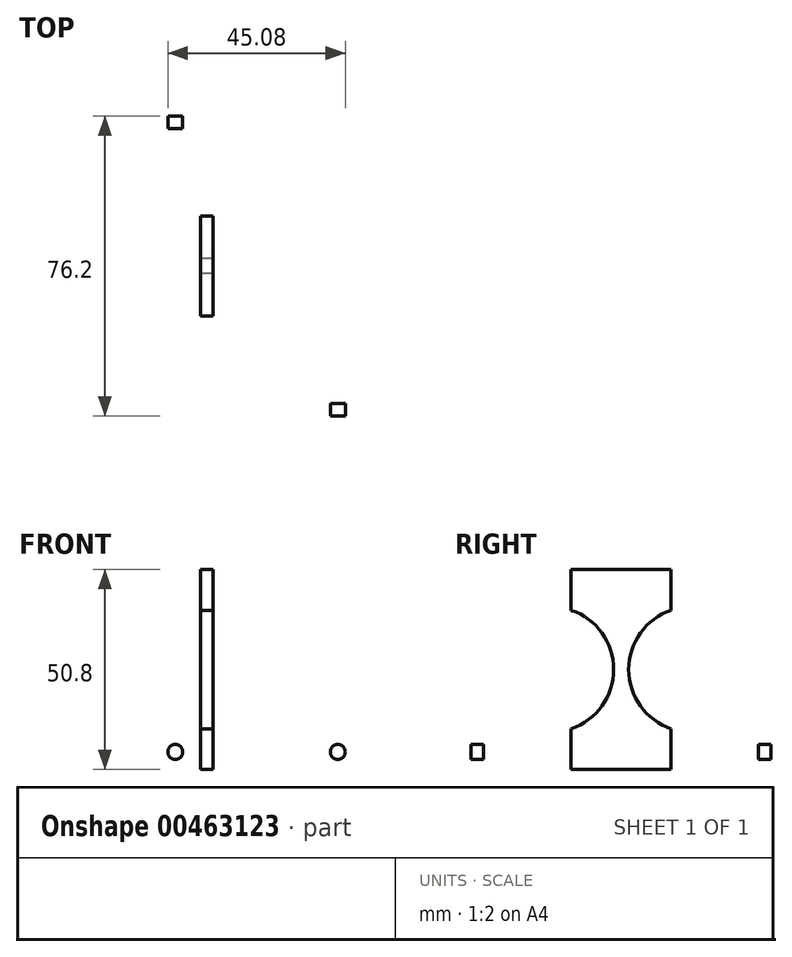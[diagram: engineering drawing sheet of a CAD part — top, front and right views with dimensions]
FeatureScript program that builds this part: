
annotation { "Feature Type Name" : "Feature", "Feature Type Description" : "" }
export const myFeature = defineFeature(function(context is Context, id is Id, definition is map)
    precondition{}
    {
        {
            var Q0;
            Q0=qCreatedBy(makeId("Top.planeOp"),FACE);
            var sketch = newSketch(context, id + "F0", { "sketchPlane" : qUnion([Q0])});
            skLineSegment(sketch, "E0.bottom", {"start": v(1.59, -38.1) * mm, "end": v(-1.59, -38.1) * mm});
            skLineSegment(sketch, "E0.top", {"start": v(1.59, 38.1) * mm, "end": v(-1.59, 38.1) * mm});
            skLineSegment(sketch, "E0.left", {"start": v(1.59, -38.1) * mm, "end": v(1.59, 38.1) * mm});
            skLineSegment(sketch, "E0.right", {"start": v(-1.59, -38.1) * mm, "end": v(-1.59, 38.1) * mm});
            skPoint(sketch, "E0.middle", {"position": v(0, 0) * mm});
            skLineSegment(sketch, "E1.bottom", {"start": v(1.59, -38.1) * mm, "end": v(39.69, -38.1) * mm});
            skLineSegment(sketch, "E1.top", {"start": v(1.59, -34.93) * mm, "end": v(39.69, -34.92) * mm});
            skLineSegment(sketch, "E1.left", {"start": v(1.59, -38.1) * mm, "end": v(1.59, -34.93) * mm});
            skLineSegment(sketch, "E1.right", {"start": v(39.69, -38.1) * mm, "end": v(39.69, -34.93) * mm});
            skLineSegment(sketch, "E2.bottom", {"start": v(-1.59, 38.1) * mm, "end": v(-14.29, 38.1) * mm});
            skLineSegment(sketch, "E2.top", {"start": v(-1.59, 34.93) * mm, "end": v(-14.29, 34.93) * mm});
            skLineSegment(sketch, "E2.left", {"start": v(-1.59, 38.1) * mm, "end": v(-1.59, 34.93) * mm});
            skLineSegment(sketch, "E2.right", {"start": v(-14.29, 38.1) * mm, "end": v(-14.29, 34.93) * mm});
            skSolve(sketch);
        }
        {
            var Q0;
            Q0=makeQuery(id+"F0.imprint","IMPRINT",FACE,{"disambiguationData":[TD([[makeQuery(id+"F0.imprint","IMPRINT",EDGE,{"derivedFrom":sQuery(id+"F0.wireOp",EDGE,"E1.bottom")}),1.0]])]});
            var Q1;
            Q1=makeQuery(id+"F0.imprint","IMPRINT",FACE,{"disambiguationData":[TD([[makeQuery(id+"F0.imprint","IMPRINT",EDGE,{"derivedFrom":sQuery(id+"F0.wireOp",EDGE,"E0.bottom")}),-1.0]])]});
            var Q2;
            Q2=makeQuery(id+"F0.imprint","IMPRINT",FACE,{"disambiguationData":[TD([[makeQuery(id+"F0.imprint","IMPRINT",EDGE,{"derivedFrom":sQuery(id+"F0.wireOp",EDGE,"E2.bottom")}),1.0]])]});
            extrude(context, id + "F1", {"entities" : qUnion([Q0, Q1, Q2]), "depth" : 50.8 * mm});
        }
        {
            var Q0;
            Q0=makeQuery(id+"F1.opExtrude","SWEPT_FACE",FACE,{"disambiguationData":[OSD([sQuery(id+"F0.wireOp",EDGE,"E0.right")])]});
            var sketch = newSketch(context, id + "F2", { "sketchPlane" : qUnion([Q0])});
            skCircle(sketch, "E3", {"center": v(-17.78, 25.4) * mm, "radius": 15.88 * mm});
            skPoint(sketch, "E3.centerSnap0", {"position": v(-34.93, 25.4) * mm});
            skCircle(sketch, "E4", {"center": v(17.78, 25.4) * mm, "radius": 15.88 * mm});
            skPoint(sketch, "E4.centerSnap0", {"position": v(38.1, 25.4) * mm});
            skSolve(sketch);
        }
        {
            var Q0;
            Q0=makeQuery(id+"F2.imprint","IMPRINT",FACE,{"disambiguationData":[TD([[makeQuery(id+"F2.imprint","IMPRINT",EDGE,{"derivedFrom":sQuery(id+"F2.wireOp",EDGE,"E4")}),1.0]])]});
            var Q1;
            Q1=makeQuery(id+"F2.imprint","IMPRINT",FACE,{"disambiguationData":[TD([[makeQuery(id+"F2.imprint","IMPRINT",EDGE,{"derivedFrom":sQuery(id+"F2.wireOp",EDGE,"E3")}),1.0]])]});
            extrude(context, id + "F3", {"entities" : qUnion([Q0, Q1]), "operationType" : NewBodyOperationType.REMOVE, "oppositeDirection" : true, "depth" : 25.4 * mm});
        }
        {
            var Q0;
            Q0=makeQuery(id+"F1.opExtrude","SWEPT_FACE",FACE,{"disambiguationData":[OSD([sQuery(id+"F0.wireOp",EDGE,"E0.bottom"),sQuery(id+"F0.wireOp",EDGE,"E1.bottom")])]});
            var sketch = newSketch(context, id + "F4", { "sketchPlane" : qUnion([Q0])});
            skLineSegment(sketch, "E5", {"start": v(39.69, 25.4) * mm, "end": v(32.02, 25.4) * mm});
            skCircle(sketch, "E6", {"center": v(33.34, 46.36) * mm, "radius": 1.9 * mm});
            skCircle(sketch, "E7.MirrorC", {"center": v(33.34, 4.44) * mm, "radius": 1.9 * mm});
            skSolve(sketch);
        }
        {
            var Q0;
            Q0=makeQuery(id+"F4.imprint","IMPRINT",FACE,{"disambiguationData":[TD([[makeQuery(id+"F4.imprint","IMPRINT",EDGE,{"derivedFrom":sQuery(id+"F4.wireOp",EDGE,"E6")}),1.0]])]});
            var Q1;
            Q1=makeQuery(id+"F4.imprint","IMPRINT",FACE,{"disambiguationData":[TD([[makeQuery(id+"F4.imprint","IMPRINT",EDGE,{"derivedFrom":sQuery(id+"F4.wireOp",EDGE,"E7.MirrorC")}),-1.0]])]});
            extrude(context, id + "F5", {"entities" : qUnion([Q0, Q1]), "operationType" : NewBodyOperationType.REMOVE, "oppositeDirection" : true, "depth" : 25.4 * mm});
        }
        {
            var Q0;
            Q0=makeQuery(id+"F1.opExtrude","SWEPT_FACE",FACE,{"disambiguationData":[OSD([sQuery(id+"F0.wireOp",EDGE,"E0.top"),sQuery(id+"F0.wireOp",EDGE,"E2.bottom")])]});
            var sketch = newSketch(context, id + "F6", { "sketchPlane" : qUnion([Q0])});
            skLineSegment(sketch, "E8", {"start": v(14.29, 25.4) * mm, "end": v(7.94, 25.4) * mm});
            skCircle(sketch, "E9", {"center": v(7.94, 46.36) * mm, "radius": 1.9 * mm});
            skCircle(sketch, "E10.MirrorC", {"center": v(7.94, 4.44) * mm, "radius": 1.9 * mm});
            skSolve(sketch);
        }
        {
            var Q0;
            Q0=makeQuery(id+"F6.imprint","IMPRINT",FACE,{"disambiguationData":[TD([[makeQuery(id+"F6.imprint","IMPRINT",EDGE,{"derivedFrom":sQuery(id+"F6.wireOp",EDGE,"E10.MirrorC")}),-1.0]])]});
            var Q1;
            Q1=makeQuery(id+"F6.imprint","IMPRINT",FACE,{"disambiguationData":[TD([[makeQuery(id+"F6.imprint","IMPRINT",EDGE,{"derivedFrom":sQuery(id+"F6.wireOp",EDGE,"E9")}),1.0]])]});
            extrude(context, id + "F7", {"entities" : qUnion([Q0, Q1]), "operationType" : NewBodyOperationType.REMOVE, "oppositeDirection" : true, "depth" : 25.4 * mm});
        }
    });
